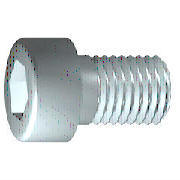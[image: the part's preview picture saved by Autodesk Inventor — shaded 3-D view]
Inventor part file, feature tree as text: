
AUTODESK INVENTOR PART (.ipt)
format: ipt  version: 2017 (Build 210142000, 142)  size: 183,808 bytes
history: native  units: mm (DEFAULTED — no unit token found)
features: sketch x2, extrude x1, plane x1, fillet x1
ambient origin geometry x7: Origin, YZ Plane, XY Plane, X Axis, Y Axis, Z Axis, Center Point
bodies: Solid1 (feature_tree), Body (feature_tree)
feature tree (5):
  extrude  "Slot"  Depth=1.5876mm
  plane  "Work Plane1"
  fillet  "Fillet2"  Radius=3.175mm
  sketch  "Sketch1"  dims[d1=19.05mm d2=1.5876mm d3=3.175mm]
  sketch  "Sketch2"  dims[d4=1.4478mm d5=60.0deg d6=3.175mm d7=3.175mm d8=2.756963mm d9=5.207mm d10=90.0deg d11=10.0mm d12=0.0mm d13=19.05mm d14=0.0mm d15=0.37846mm d16=0.37846mm d17=0.3048mm d19=0.0mm d26=38.1mm d27=45.0deg d28=0.0mm d29=0.0mm d30=0.127mm]
